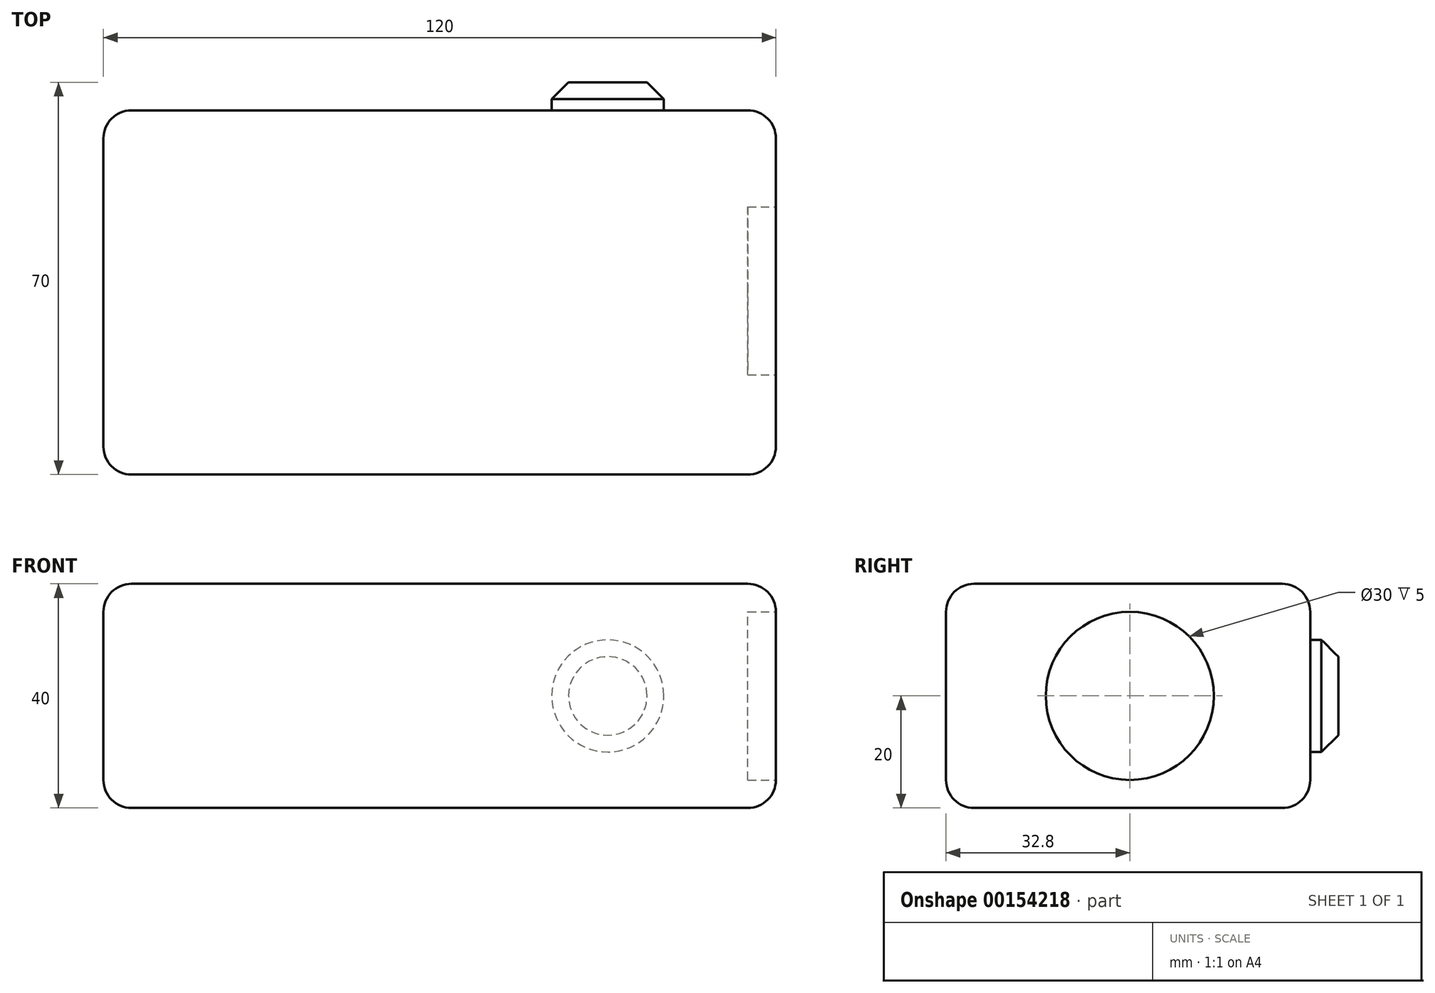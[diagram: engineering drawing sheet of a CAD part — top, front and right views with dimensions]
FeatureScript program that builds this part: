
annotation { "Feature Type Name" : "Feature", "Feature Type Description" : "" }
export const myFeature = defineFeature(function(context is Context, id is Id, definition is map)
    precondition{}
    {
        {
            var Q0;
            Q0=qCreatedBy(makeId("Top.planeOp"),FACE);
            var sketch = newSketch(context, id + "F0", { "sketchPlane" : qUnion([Q0])});
            skLineSegment(sketch, "E0.bottom", {"start": v(-60, 32.2) * mm, "end": v(60, 32.2) * mm});
            skLineSegment(sketch, "E0.top", {"start": v(-60, -32.8) * mm, "end": v(60, -32.8) * mm});
            skLineSegment(sketch, "E0.left", {"start": v(-60, 32.2) * mm, "end": v(-60, -32.8) * mm});
            skLineSegment(sketch, "E0.right", {"start": v(60, 32.2) * mm, "end": v(60, -32.8) * mm});
            skPoint(sketch, "E0.middle", {"position": v(0, -0.3) * mm});
            skSolve(sketch);
        }
        {
            var Q0;
            Q0 = qSketchRegion(id + "F0", true);
            extrude(context, id + "F1", {"entities" : qUnion([Q0]), "depth" : 40 * mm});
        }
        {
            var Q0;
            Q0=makeQuery(id+"F1.opExtrude","SWEPT_EDGE",EDGE,{"disambiguationData":[OSD([sQuery(id+"F0.wireOp",EDGE,"E0.top"),sQuery(id+"F0.wireOp",EDGE,"E0.left")])]});
            var Q1;
            Q1=makeQuery(id+"F1.opExtrude","SWEPT_EDGE",EDGE,{"disambiguationData":[OSD([sQuery(id+"F0.wireOp",EDGE,"E0.top"),sQuery(id+"F0.wireOp",EDGE,"E0.right")])]});
            var Q2;
            Q2=makeQuery(id+"F1.opExtrude","SWEPT_EDGE",EDGE,{"disambiguationData":[OSD([sQuery(id+"F0.wireOp",EDGE,"E0.bottom"),sQuery(id+"F0.wireOp",EDGE,"E0.right")])]});
            var Q3;
            Q3=makeQuery(id+"F1.opExtrude","SWEPT_EDGE",EDGE,{"disambiguationData":[OSD([sQuery(id+"F0.wireOp",EDGE,"E0.bottom"),sQuery(id+"F0.wireOp",EDGE,"E0.left")])]});
            var Q4;
            Q4=makeQuery(id+"F1.opExtrude","CAP_EDGE",EDGE,{"disambiguationData":[OSD([sQuery(id+"F0.wireOp",EDGE,"E0.bottom")])],"isStart":false});
            var Q5;
            Q5=makeQuery(id+"F1.opExtrude","CAP_EDGE",EDGE,{"disambiguationData":[OSD([sQuery(id+"F0.wireOp",EDGE,"E0.right")])],"isStart":false});
            var Q6;
            Q6=makeQuery(id+"F1.opExtrude","CAP_EDGE",EDGE,{"disambiguationData":[OSD([sQuery(id+"F0.wireOp",EDGE,"E0.top")])],"isStart":false});
            var Q7;
            Q7=makeQuery(id+"F1.opExtrude","CAP_EDGE",EDGE,{"disambiguationData":[OSD([sQuery(id+"F0.wireOp",EDGE,"E0.left")])],"isStart":false});
            var Q8;
            Q8=makeQuery(id+"F1.opExtrude","CAP_EDGE",EDGE,{"disambiguationData":[OSD([sQuery(id+"F0.wireOp",EDGE,"E0.bottom")])],"isStart":true});
            var Q9;
            Q9=makeQuery(id+"F1.opExtrude","CAP_EDGE",EDGE,{"disambiguationData":[OSD([sQuery(id+"F0.wireOp",EDGE,"E0.top")])],"isStart":true});
            var Q10;
            Q10=makeQuery(id+"F1.opExtrude","CAP_EDGE",EDGE,{"disambiguationData":[OSD([sQuery(id+"F0.wireOp",EDGE,"E0.left")])],"isStart":true});
            var Q11;
            Q11=makeQuery(id+"F1.opExtrude","CAP_EDGE",EDGE,{"disambiguationData":[OSD([sQuery(id+"F0.wireOp",EDGE,"E0.right")])],"isStart":true});
            fillet(context, id + "F2", {"entities" : qUnion([Q0, Q1, Q2, Q3, Q4, Q5, Q6, Q7, Q8, Q9, Q10, Q11]), "radius" : 5 * mm, "tangentPropagation" : true, "allowEdgeOverflow" : false});
        }
        {
            var Q0;
            Q0=makeQuery(id+"F1.opExtrude","SWEPT_FACE",FACE,{"disambiguationData":[OSD([sQuery(id+"F0.wireOp",EDGE,"E0.right")])]});
            var sketch = newSketch(context, id + "F3", { "sketchPlane" : qUnion([Q0])});
            skCircle(sketch, "E1", {"center": v(0, 20) * mm, "radius": 15 * mm});
            skPoint(sketch, "E1.centerSnap0", {"position": v(-27.8, 20) * mm});
            skSolve(sketch);
        }
        {
            var Q0;
            Q0 = qSketchRegion(id + "F3", true);
            extrude(context, id + "F4", {"entities" : qUnion([Q0]), "operationType" : NewBodyOperationType.REMOVE, "oppositeDirection" : true, "depth" : 5 * mm});
        }
        {
            var Q0;
            Q0=makeQuery(id+"F1.opExtrude","SWEPT_FACE",FACE,{"disambiguationData":[OSD([sQuery(id+"F0.wireOp",EDGE,"E0.bottom")])]});
            var sketch = newSketch(context, id + "F5", { "sketchPlane" : qUnion([Q0])});
            skCircle(sketch, "E2", {"center": v(-30, 20) * mm, "radius": 10 * mm});
            skSolve(sketch);
        }
        {
            var Q0;
            Q0=makeQuery(id+"F5.imprint","IMPRINT",FACE,{"disambiguationData":[TD([[makeQuery(id+"F5.imprint","IMPRINT",EDGE,{"derivedFrom":sQuery(id+"F5.wireOp",EDGE,"E2")}),1.0]])]});
            extrude(context, id + "F6", {"entities" : qUnion([Q0]), "operationType" : NewBodyOperationType.ADD, "depth" : 5 * mm});
        }
        {
            var Q0;
            Q0=makeQuery(id+"F6.opExtrude","CAP_EDGE",EDGE,{"disambiguationData":[OSD([sQuery(id+"F5.wireOp",EDGE,"E2")])],"isStart":false});
            chamfer(context, id + "F7", {"entities" : qUnion([Q0]), "width" : 3 * mm, "tangentPropagation" : true});
        }
    });
